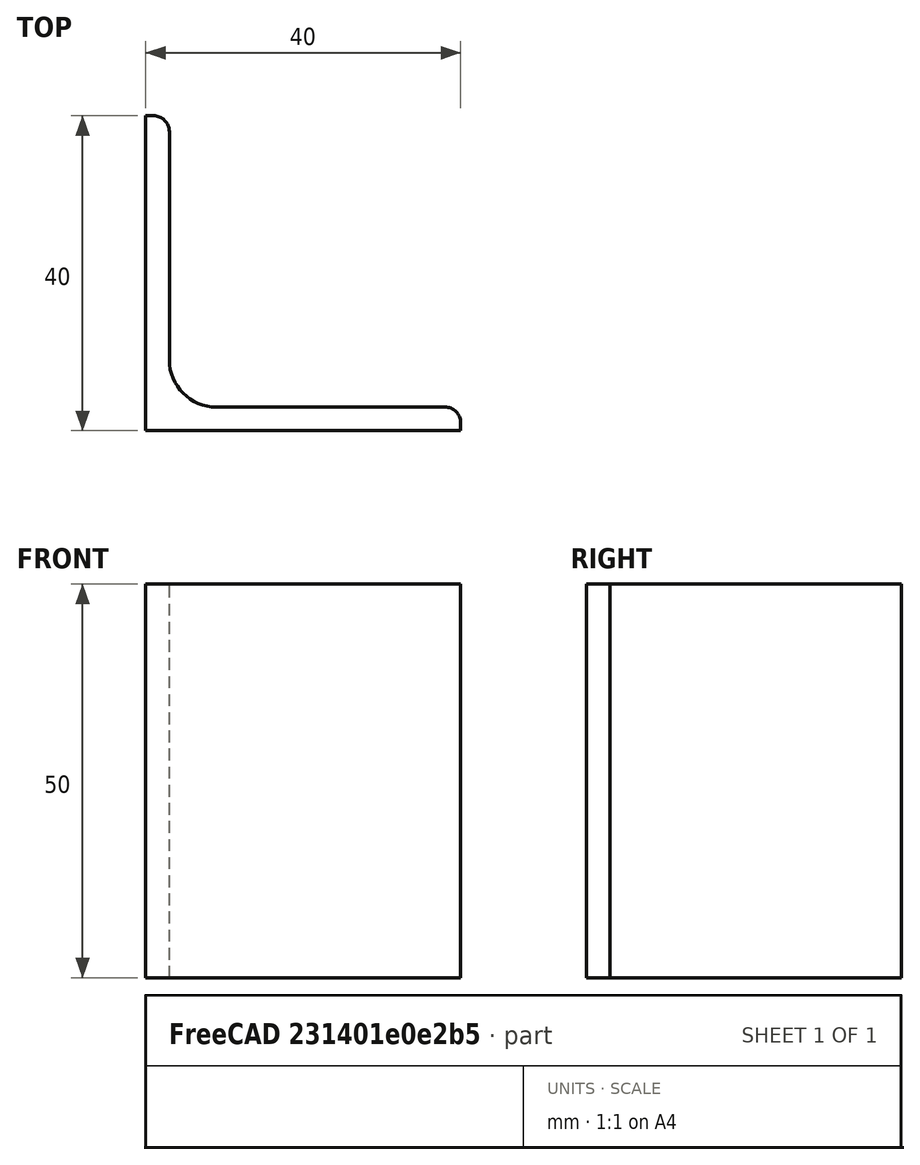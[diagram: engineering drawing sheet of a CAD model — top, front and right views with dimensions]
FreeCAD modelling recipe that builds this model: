
FCSTD DOCUMENT  (FreeCAD 0.15R4671 (Git))
Label: Angle Bar L40x40x3 EN10056 S235JR
License: All rights reserved
LicenseURL: http://en.wikipedia.org/wiki/All_rights_reserved
objects: Sketcher::SketchObject×1, Part::Extrusion×1
note: 2 computed .brp shape members not serialized (recipe doc carries the construction recipe); baked Part::Feature solids carry a one-line shape summary decoded from their .brp

FEATURE [Sketcher::SketchObject] Sketch
  sketch-geometry (9):
    g0: LineSegment StartX=0 StartY=0 StartZ=0 EndX=40 EndY=0 EndZ=0
    g1: LineSegment StartX=40 StartY=0 StartZ=0 EndX=40 EndY=1 EndZ=0
    g2: LineSegment StartX=38 StartY=3 StartZ=0 EndX=9 EndY=3 EndZ=0
    g3: LineSegment StartX=0 StartY=0 StartZ=0 EndX=0 EndY=40 EndZ=0
    g4: LineSegment StartX=0 StartY=40 StartZ=0 EndX=1 EndY=40 EndZ=0
    g5: LineSegment StartX=3 StartY=38 StartZ=0 EndX=3 EndY=9 EndZ=0
    g6: ArcOfCircle CenterX=9 CenterY=9 CenterZ=0 NormalX=0 NormalY=0 NormalZ=1 Radius=6 StartAngle=3.14159 EndAngle=4.71239
    g7: ArcOfCircle CenterX=1 CenterY=38 CenterZ=0 NormalX=0 NormalY=0 NormalZ=1 Radius=2 StartAngle=0 EndAngle=1.5708
    g8: ArcOfCircle CenterX=38 CenterY=1 CenterZ=0 NormalX=0 NormalY=0 NormalZ=1 Radius=2 StartAngle=0 EndAngle=1.5708
  constraints (23):
    c: Coincident(g0,g-1)
    c: Horizontal(g0)
    c: Coincident(g1,g0)
    c: Vertical(g1)
    c: Horizontal(g2)
    c: Coincident(g3,g-1)
    c: Vertical(g3)
    c: Coincident(g4,g3)
    c: Horizontal(g4)
    c: Vertical(g5)
    c: Tangent(g5,g6) = -1.5708
    c: Tangent(g2,g6) = 1.5708
    c: Tangent(g4,g7) = 1.5708
    c: Tangent(g5,g7) = 1.5708
    c: Tangent(g2,g8) = -1.5708
    c: Tangent(g1,g8) = -1.5708
    c: DistanceX(g0) = 40
    c: DistanceY(g3) = 40
    c: DistanceY(g0,g2) = 3
    c: DistanceX(g3,g5) = 3
    c: Radius(g6) = 6
    c: Radius(g8) = 2
    c: Radius(g7) = 2
FEATURE [Part::Extrusion] Extrude  label="Angle Bar L40x40x3 EN10056 S235JR"
  Base = -> Sketch
  Dir = (0,0,50)
  Solid = true
